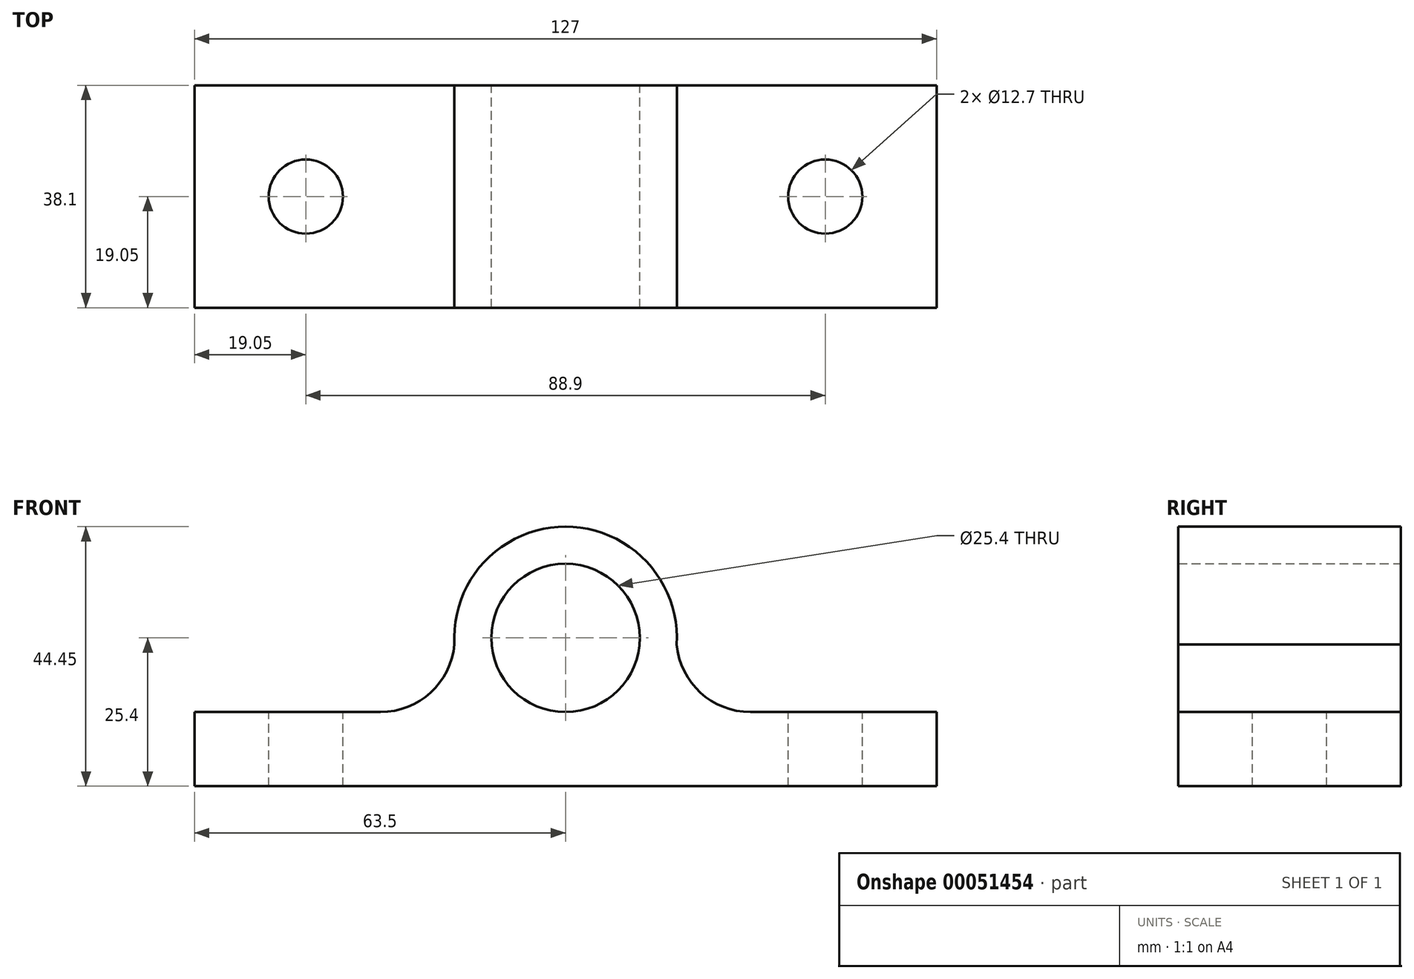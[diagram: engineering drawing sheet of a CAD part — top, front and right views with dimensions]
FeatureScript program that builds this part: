
annotation { "Feature Type Name" : "Feature", "Feature Type Description" : "" }
export const myFeature = defineFeature(function(context is Context, id is Id, definition is map)
    precondition{}
    {
        {
            var Q0;
            Q0=qCreatedBy(makeId("Front.planeOp"),FACE);
            var sketch = newSketch(context, id + "F0", { "sketchPlane" : qUnion([Q0])});
            skLineSegment(sketch, "E0.bottom", {"start": v(-65, 19.5) * mm, "end": v(-33.16, 19.5) * mm});
            skLineSegment(sketch, "E0.top", {"start": v(-65, 6.8) * mm, "end": v(62, 6.8) * mm});
            skLineSegment(sketch, "E0.left", {"start": v(-65, 19.5) * mm, "end": v(-65, 6.8) * mm});
            skLineSegment(sketch, "E0.right", {"start": v(62, 19.5) * mm, "end": v(62, 6.8) * mm});
            skLineSegment(sketch, "E1.0", {"start": v(-20.55, 32.2) * mm, "end": v(17.55, 32.2) * mm, "construction": true});
            skCircle(sketch, "E2", {"center": v(-1.5, 32.2) * mm, "radius": 12.7 * mm});
            skArc(sketch, "E3", {"start": v(17.52, 31.06) * mm, "mid": v(-1.5, 51.25) * mm, "end": v(-20.52, 31.06) * mm});
            skArc(sketch, "E4", {"start": v(-33.16, 19.5) * mm, "mid": v(-23.79, 23.63) * mm, "end": v(-20.52, 33.34) * mm});
            skLineSegment(sketch, "E5.trimOffspring", {"start": v(30.16, 19.5) * mm, "end": v(62, 19.5) * mm});
            skLineSegment(sketch, "E6", {"start": v(-1.5, 32.2) * mm, "end": v(-1.5, 51.25) * mm, "construction": true});
            skArc(sketch, "E7.MirrorCS", {"start": v(30.16, 19.5) * mm, "mid": v(20.79, 23.63) * mm, "end": v(17.52, 33.34) * mm});
            skPoint(sketch, "E8.orphan", {"position": v(62, 32.2) * mm});
            skPoint(sketch, "E9.orphan", {"position": v(-65, 32.2) * mm});
            skSolve(sketch);
        }
        {
            var Q0;
            Q0 = qSketchRegion(id + "F0", true);
            extrude(context, id + "F1", {"entities" : qUnion([Q0]), "depth" : 38.1 * mm});
        }
        {
            var Q0;
            Q0=makeQuery(id+"F1.opExtrude","SWEPT_FACE",FACE,{"disambiguationData":[OSD([sQuery(id+"F0.wireOp",EDGE,"E5.trimOffspring")])]});
            var sketch = newSketch(context, id + "F2", { "sketchPlane" : qUnion([Q0])});
            skCircle(sketch, "E10", {"center": v(-45.95, -19.05) * mm, "radius": 6.35 * mm});
            skLineSegment(sketch, "E11.0", {"start": v(-45.95, -38.1) * mm, "end": v(-45.95, 0) * mm, "construction": true});
            skLineSegment(sketch, "E12.0", {"start": v(42.95, -38.1) * mm, "end": v(42.95, 0) * mm, "construction": true});
            skCircle(sketch, "E13", {"center": v(42.95, -19.05) * mm, "radius": 6.35 * mm});
            skSolve(sketch);
        }
        {
            var Q0;
            Q0=makeQuery(id+"F2.imprint","IMPRINT",FACE,{"disambiguationData":[TD([[makeQuery(id+"F2.imprint","IMPRINT",EDGE,{"derivedFrom":sQuery(id+"F2.wireOp",EDGE,"E13")}),1.0]])]});
            var Q1;
            Q1=makeQuery(id+"F2.imprint","IMPRINT",FACE,{"disambiguationData":[TD([[makeQuery(id+"F2.imprint","IMPRINT",EDGE,{"derivedFrom":sQuery(id+"F2.wireOp",EDGE,"E10")}),1.0]])]});
            extrude(context, id + "F3", {"entities" : qUnion([Q0, Q1]), "operationType" : NewBodyOperationType.REMOVE, "endBound" : BoundingType.THROUGH_ALL, "oppositeDirection" : true, "depth" : 25.4 * mm});
        }
    });
